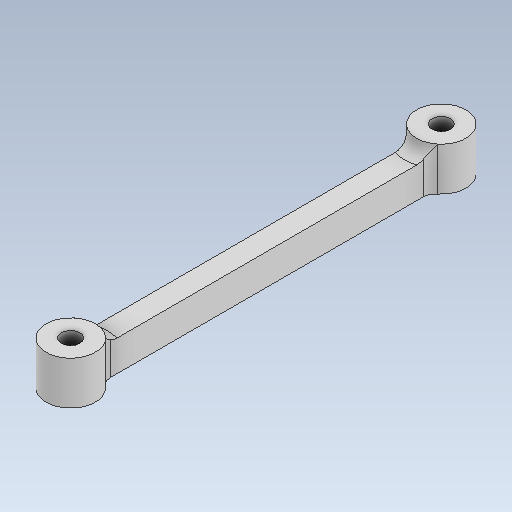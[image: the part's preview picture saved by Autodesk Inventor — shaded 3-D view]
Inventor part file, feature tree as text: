
AUTODESK INVENTOR PART (.ipt)
format: ipt  version: 2023 (Build 270158000, 158)  size: 122,880 bytes
history: native  units: mm
features: other x3, sketch x3
ambient origin geometry x8: Origin, YZ Plane, XZ Plane, XY Plane, X Axis, Y Axis, Z Axis, Center Point
bodies: Solid1 (feature_tree)
feature tree (6):
  other  "leg_link_3_m.ipt"
  other  "Solid1::leg_link_3_m.ipt"
  other  "TaggingFeature1"
  sketch  "Sketch1"  dims[d0=10.0mm]
  sketch  "Sketch2"
  sketch  "Sketch3"
